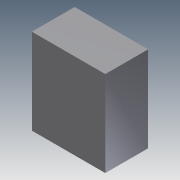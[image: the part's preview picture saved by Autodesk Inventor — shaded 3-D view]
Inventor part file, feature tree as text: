
AUTODESK INVENTOR PART (.ipt)
format: ipt  version: 2011 (Build 150239000, 239)  size: 68,096 bytes
history: native  units: in
note: dims shown in document units (in); Inventor stores cm internally (conversion verified against a paired STEP export)
features: extrude x1, sketch x1
ambient origin geometry x8: Origin, YZ Plane, XZ Plane, XY Plane, X Axis, Y Axis, Z Axis, Center Point
bodies: Solid1 (feature_tree)
feature tree (2):
  extrude  "Extrusion1"  Depth=7.0in
  sketch  "Sketch1"  dims[d0=6.0in d1=7.0in d2=3.5in d3=0.0in]
